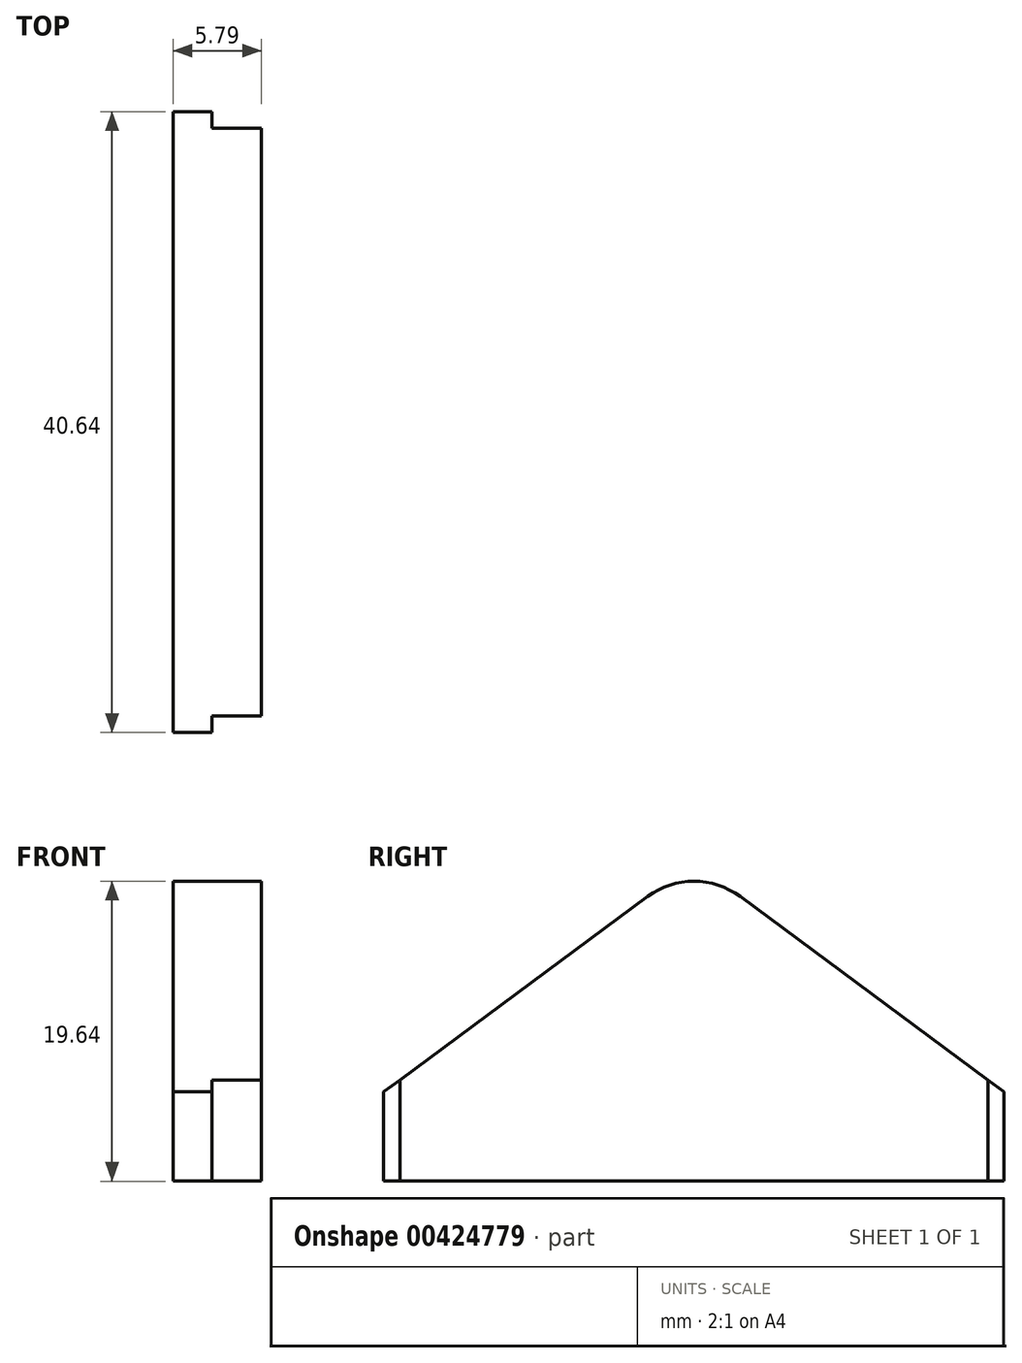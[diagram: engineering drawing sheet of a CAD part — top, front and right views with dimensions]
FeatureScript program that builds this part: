
annotation { "Feature Type Name" : "Feature", "Feature Type Description" : "" }
export const myFeature = defineFeature(function(context is Context, id is Id, definition is map)
    precondition{}
    {
        {
            var Q0;
            Q0=qCreatedBy(makeId("Right.planeOp"),FACE);
            var sketch = newSketch(context, id + "F0", { "sketchPlane" : qUnion([Q0])});
            skArc(sketch, "E0", {"start": v(3.02, 13.13) * mm, "mid": v(1.6, 13.87) * mm, "end": v(0, 14.12) * mm});
            skLineSegment(sketch, "E1", {"start": v(3.02, 13.13) * mm, "end": v(20.32, 0.33) * mm});
            skLineSegment(sketch, "E2", {"start": v(20.32, 0.33) * mm, "end": v(20.32, -5.52) * mm});
            skLineSegment(sketch, "E3.MirrorCS", {"start": v(-20.32, 0.33) * mm, "end": v(-20.32, -5.52) * mm});
            skLineSegment(sketch, "E4.MirrorCS", {"start": v(-3.02, 13.13) * mm, "end": v(-20.32, 0.33) * mm});
            skArc(sketch, "E5.MirrorCS", {"start": v(-3.02, 13.13) * mm, "mid": v(-1.6, 13.87) * mm, "end": v(0, 14.12) * mm});
            skLineSegment(sketch, "E6", {"start": v(-20.32, -5.52) * mm, "end": v(20.32, -5.52) * mm});
            skSolve(sketch);
        }
        {
            var Q0;
            Q0=makeQuery(id+"F0.imprint","IMPRINT",FACE,{"disambiguationData":[TD([[makeQuery(id+"F0.imprint","IMPRINT",EDGE,{"derivedFrom":sQuery(id+"F0.wireOp",EDGE,"E0")}),1.0]])]});
            extrude(context, id + "F1", {"entities" : qUnion([Q0]), "depth" : 5.8 * mm});
        }
        {
            var Q0;
            Q0=makeQuery(id+"F1.opExtrude","CAP_FACE",FACE,{"disambiguationData":[OSD([sQuery(id+"F0.wireOp",EDGE,"E0"),sQuery(id+"F0.wireOp",EDGE,"E1"),sQuery(id+"F0.wireOp",EDGE,"E2"),sQuery(id+"F0.wireOp",EDGE,"HqgXSdXz-I8LB-OIzT-85Jw-HgCfuJsVfkn1"),sQuery(id+"F0.wireOp",EDGE,"s013FR44-5wnw-u0Eq-BKtS-vUDOPIgE5DMX"),sQuery(id+"F0.wireOp",EDGE,"4c8bd502-92ec-4371-86a4-382d24c530830.MirrorCS"),sQuery(id+"F0.wireOp",EDGE,"697efb37-2049-4ebb-98f3-d9f7ce05d3110.MirrorCS"),sQuery(id+"F0.wireOp",EDGE,"E3.MirrorCS"),sQuery(id+"F0.wireOp",EDGE,"E4.MirrorCS"),sQuery(id+"F0.wireOp",EDGE,"E5.MirrorCS")])],"isStart":false});
            var sketch = newSketch(context, id + "F2", { "sketchPlane" : qUnion([Q0])});
            skLineSegment(sketch, "E7", {"start": v(20.32, 0.33) * mm, "end": v(20.32, 0.33) * mm});
            skLineSegment(sketch, "E8", {"start": v(20.32, 0.33) * mm, "end": v(19.25, 1.12) * mm});
            skLineSegment(sketch, "E9", {"start": v(19.25, 1.12) * mm, "end": v(19.25, 1.12) * mm});
            skLineSegment(sketch, "E10", {"start": v(19.25, 1.12) * mm, "end": v(20.32, 0.33) * mm});
            skLineSegment(sketch, "E11.MirrorCS", {"start": v(-19.25, 1.12) * mm, "end": v(-19.25, 1.12) * mm});
            skLineSegment(sketch, "E12.MirrorCS", {"start": v(-20.32, 0.33) * mm, "end": v(-19.25, 1.12) * mm});
            skLineSegment(sketch, "E13.MirrorCS", {"start": v(-20.32, 0.33) * mm, "end": v(-20.32, 0.33) * mm});
            skLineSegment(sketch, "E14.MirrorCS", {"start": v(-19.25, 1.12) * mm, "end": v(-20.32, 0.33) * mm});
            skLineSegment(sketch, "E15", {"start": v(19.25, 1.12) * mm, "end": v(19.25, -5.52) * mm});
            skLineSegment(sketch, "E16", {"start": v(19.25, -5.52) * mm, "end": v(20.32, -5.52) * mm});
            skLineSegment(sketch, "E17", {"start": v(20.32, -5.52) * mm, "end": v(20.32, 0.33) * mm});
            skLineSegment(sketch, "E18.MirrorCS", {"start": v(-19.25, 1.12) * mm, "end": v(-19.25, -5.52) * mm});
            skLineSegment(sketch, "E19.MirrorCS", {"start": v(-20.32, -5.52) * mm, "end": v(-20.32, 0.33) * mm});
            skLineSegment(sketch, "E20.MirrorCS", {"start": v(-19.25, -5.52) * mm, "end": v(-20.32, -5.52) * mm});
            skSolve(sketch);
        }
        {
            var Q0;
            Q0=qSketchRegion(id+"F2",true);
            extrude(context, id + "F3", {"entities" : qUnion([Q0]), "operationType" : NewBodyOperationType.REMOVE, "oppositeDirection" : true, "depth" : 3.25 * mm});
        }
    });
